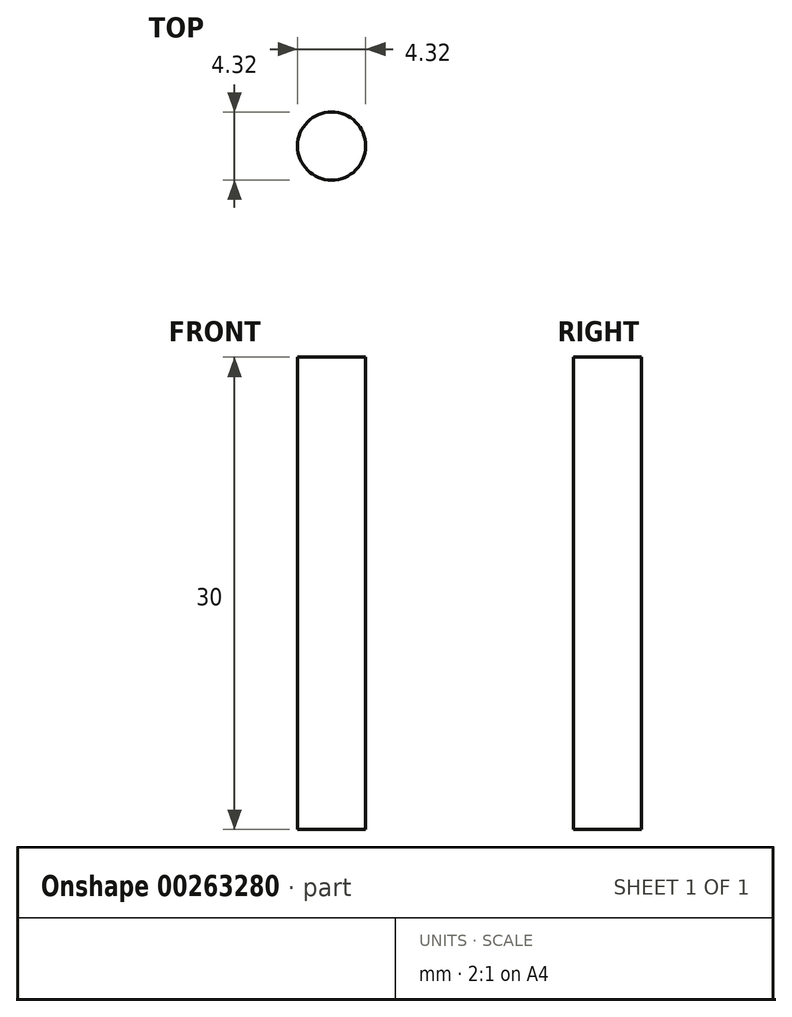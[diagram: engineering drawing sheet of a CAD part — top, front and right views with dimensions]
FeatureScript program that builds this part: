
annotation { "Feature Type Name" : "Feature", "Feature Type Description" : "" }
export const myFeature = defineFeature(function(context is Context, id is Id, definition is map)
    precondition{}
    {
        {
            var Q0;
            Q0=qCreatedBy(makeId("Top.planeOp"),FACE);
            var sketch = newSketch(context, id + "F0", { "sketchPlane" : qUnion([Q0])});
            skCircle(sketch, "E0", {"center": v(0, 0) * mm, "radius": 2.16 * mm});
            skSolve(sketch);
        }
        {
            var Q0;
            Q0 = qSketchRegion(id + "F0", true);
            extrude(context, id + "F1", {"entities" : qUnion([Q0]), "depth" : 30 * mm});
        }
    });
